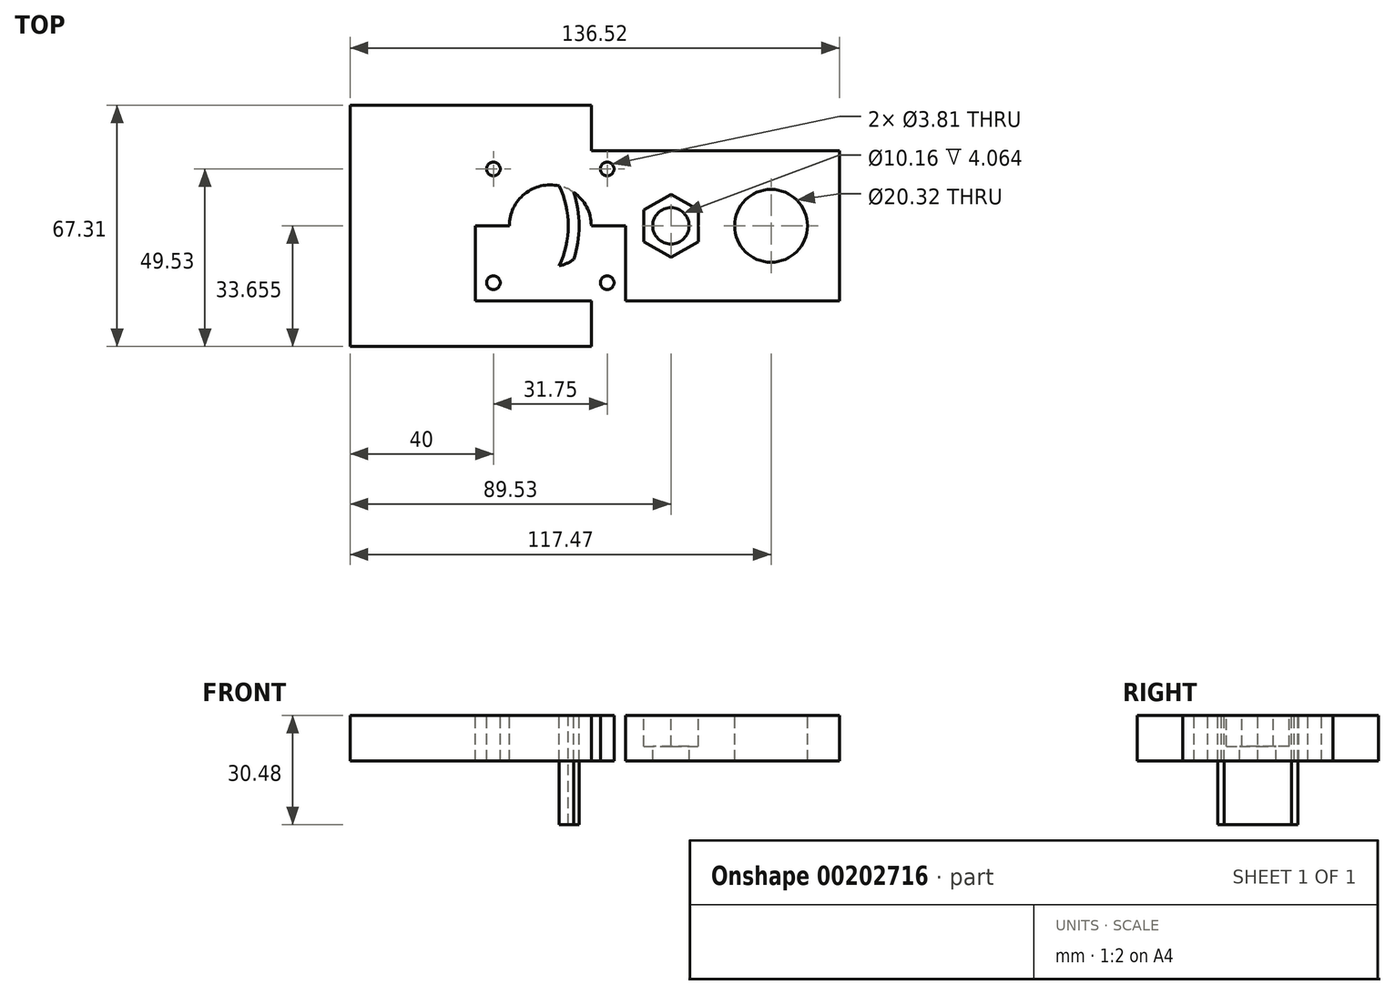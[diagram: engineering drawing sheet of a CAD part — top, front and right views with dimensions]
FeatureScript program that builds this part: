
annotation { "Feature Type Name" : "Feature", "Feature Type Description" : "" }
export const myFeature = defineFeature(function(context is Context, id is Id, definition is map)
    precondition{}
    {
        {
            var Q0;
            Q0=qCreatedBy(makeId("Top.planeOp"),FACE);
            var sketch = newSketch(context, id + "F0", { "sketchPlane" : qUnion([Q0])});
            skLineSegment(sketch, "E0.bottom", {"start": v(0, 0) * mm, "end": v(101.6, 0) * mm});
            skLineSegment(sketch, "E0.top", {"start": v(0, 41.91) * mm, "end": v(101.6, 41.91) * mm});
            skLineSegment(sketch, "E0.left", {"start": v(0, 0) * mm, "end": v(0, 41.91) * mm});
            skLineSegment(sketch, "E0.right", {"start": v(101.6, 0) * mm, "end": v(101.6, 41.91) * mm});
            skSolve(sketch);
        }
        {
            var Q0;
            Q0=makeQuery(id+"F0.imprint","IMPRINT",FACE,{"disambiguationData":[TD([[makeQuery(id+"F0.imprint","IMPRINT",EDGE,{"derivedFrom":sQuery(id+"F0.wireOp",EDGE,"E0.bottom")}),1.0]])]});
            extrude(context, id + "F1", {"entities" : qUnion([Q0]), "depth" : 12.7 * mm});
        }
        {
            var Q0;
            Q0=makeQuery(id+"F1.opExtrude","CAP_FACE",FACE,{"disambiguationData":[OSD([sQuery(id+"F0.wireOp",EDGE,"E0.bottom"),sQuery(id+"F0.wireOp",EDGE,"E0.top"),sQuery(id+"F0.wireOp",EDGE,"E0.left"),sQuery(id+"F0.wireOp",EDGE,"E0.right")])],"isStart":false});
            var sketch = newSketch(context, id + "F2", { "sketchPlane" : qUnion([Q0])});
            skLineSegment(sketch, "E1", {"start": v(0, 41.91) * mm, "end": v(5.08, 41.91) * mm});
            skLineSegment(sketch, "E2", {"start": v(5.08, 41.91) * mm, "end": v(5.08, 36.83) * mm});
            skLineSegment(sketch, "E3", {"start": v(0, 20.96) * mm, "end": v(101.6, 20.96) * mm});
            skLineSegment(sketch, "E4", {"start": v(0, 41.91) * mm, "end": v(41.91, 41.91) * mm});
            skLineSegment(sketch, "E5", {"start": v(41.91, 41.91) * mm, "end": v(41.91, 0) * mm});
            skLineSegment(sketch, "E6", {"start": v(41.91, 41.91) * mm, "end": v(36.83, 41.91) * mm});
            skLineSegment(sketch, "E7", {"start": v(36.83, 41.91) * mm, "end": v(36.83, 36.83) * mm});
            skLineSegment(sketch, "E8", {"start": v(41.91, 0) * mm, "end": v(41.91, 5.08) * mm});
            skCircle(sketch, "E9", {"center": v(36.83, 36.83) * mm, "radius": 1.9 * mm});
            skCircle(sketch, "E10", {"center": v(5.08, 36.83) * mm, "radius": 1.9 * mm});
            skCircle(sketch, "E11.MirrorC", {"center": v(36.83, 5.08) * mm, "radius": 1.9 * mm});
            skCircle(sketch, "E12.MirrorC", {"center": v(5.08, 5.08) * mm, "radius": 1.9 * mm});
            skSolve(sketch);
        }
        {
            var Q0;
            Q0=makeQuery(id+"F1.opExtrude","CAP_FACE",FACE,{"disambiguationData":[OSD([sQuery(id+"F0.wireOp",EDGE,"E0.bottom"),sQuery(id+"F0.wireOp",EDGE,"E0.top"),sQuery(id+"F0.wireOp",EDGE,"E0.left"),sQuery(id+"F0.wireOp",EDGE,"E0.right")])],"isStart":false});
            var sketch = newSketch(context, id + "F3", { "sketchPlane" : qUnion([Q0])});
            skLineSegment(sketch, "E13", {"start": v(0, 41.91) * mm, "end": v(41.91, 41.91) * mm});
            skLineSegment(sketch, "E14", {"start": v(41.91, 41.91) * mm, "end": v(41.91, 0) * mm});
            skLineSegment(sketch, "E15", {"start": v(41.91, 41.91) * mm, "end": v(54.61, 41.91) * mm});
            skLineSegment(sketch, "E16", {"start": v(54.61, 41.91) * mm, "end": v(54.61, 20.96) * mm});
            skCircle(sketch, "E17", {"center": v(54.61, 20.96) * mm, "radius": 5.08 * mm});
            skSolve(sketch);
        }
        {
            var Q0;
            Q0=makeQuery(id+"F3.imprint","IMPRINT",FACE,{"disambiguationData":[TD([[makeQuery(id+"F3.imprint","IMPRINT",EDGE,{"derivedFrom":sQuery(id+"F3.wireOp",EDGE,"E17")}),1.0]])]});
            extrude(context, id + "F4", {"entities" : qUnion([Q0]), "operationType" : NewBodyOperationType.REMOVE, "endBound" : BoundingType.THROUGH_ALL, "oppositeDirection" : true, "depth" : 25.4 * mm});
        }
        {
            var Q0;
            Q0=makeQuery(id+"F1.opExtrude","CAP_FACE",FACE,{"disambiguationData":[OSD([sQuery(id+"F0.wireOp",EDGE,"E0.bottom"),sQuery(id+"F0.wireOp",EDGE,"E0.top"),sQuery(id+"F0.wireOp",EDGE,"E0.left"),sQuery(id+"F0.wireOp",EDGE,"E0.right")])],"isStart":false});
            var sketch = newSketch(context, id + "F5", { "sketchPlane" : qUnion([Q0])});
            skLineSegment(sketch, "E18", {"start": v(54.61, 20.96) * mm, "end": v(62.23, 20.96) * mm});
            skCircle(sketch, "E19.cCircle", {"center": v(54.61, 20.96) * mm, "radius": 7.62 * mm, "construction": true});
            skLineSegment(sketch, "E19.0", {"start": v(62.23, 25.35) * mm, "end": v(62.23, 16.56) * mm});
            skLineSegment(sketch, "E19.1", {"start": v(62.23, 16.56) * mm, "end": v(54.61, 12.16) * mm});
            skLineSegment(sketch, "E19.2", {"start": v(54.61, 12.16) * mm, "end": v(46.99, 16.56) * mm});
            skLineSegment(sketch, "E19.3", {"start": v(47, 16.56) * mm, "end": v(47, 25.35) * mm});
            skLineSegment(sketch, "E19.4", {"start": v(47, 25.35) * mm, "end": v(54.6, 29.75) * mm});
            skLineSegment(sketch, "E19.5", {"start": v(54.6, 29.75) * mm, "end": v(62.23, 25.35) * mm});
            skPoint(sketch, "E19.0.midPoint", {"position": v(62.23, 20.96) * mm});
            skSolve(sketch);
        }
        {
            var Q0;
            {var subQ0=sQuery(id+"F5.wireOp",EDGE,"E19.1");Q0=makeQuery(id+"F5.imprint","IMPRINT",FACE,{"disambiguationData":[TD([[makeQuery(id+"F5.imprint","IMPRINT",EDGE,{"derivedFrom":subQ0}),-1.0]])]});}
            extrude(context, id + "F6", {"entities" : qUnion([Q0]), "operationType" : NewBodyOperationType.REMOVE, "oppositeDirection" : true, "depth" : 8.64 * mm});
        }
        {
            var Q0;
            Q0=makeQuery(id+"F1.opExtrude","CAP_FACE",FACE,{"disambiguationData":[OSD([sQuery(id+"F0.wireOp",EDGE,"E0.bottom"),sQuery(id+"F0.wireOp",EDGE,"E0.top"),sQuery(id+"F0.wireOp",EDGE,"E0.left"),sQuery(id+"F0.wireOp",EDGE,"E0.right")])],"isStart":false});
            var sketch = newSketch(context, id + "F7", { "sketchPlane" : qUnion([Q0])});
            skLineSegment(sketch, "E20", {"start": v(101.6, 20.96) * mm, "end": v(82.55, 20.96) * mm});
            skPoint(sketch, "E20.endSnap0", {"position": v(101.6, 20.96) * mm});
            skCircle(sketch, "E21", {"center": v(82.55, 20.96) * mm, "radius": 10.16 * mm});
            skSolve(sketch);
        }
        {
            var Q0;
            Q0=makeQuery(id+"F7.imprint","IMPRINT",FACE,{"disambiguationData":[TD([[makeQuery(id+"F7.imprint","IMPRINT",EDGE,{"derivedFrom":sQuery(id+"F7.wireOp",EDGE,"E21")}),1.0]])]});
            extrude(context, id + "F8", {"entities" : qUnion([Q0]), "operationType" : NewBodyOperationType.REMOVE, "endBound" : BoundingType.THROUGH_ALL, "oppositeDirection" : true, "depth" : 25.4 * mm});
        }
        {
            var Q0;
            Q0=makeQuery(id+"F1.opExtrude","CAP_FACE",FACE,{"disambiguationData":[OSD([sQuery(id+"F0.wireOp",EDGE,"E0.bottom"),sQuery(id+"F0.wireOp",EDGE,"E0.top"),sQuery(id+"F0.wireOp",EDGE,"E0.left"),sQuery(id+"F0.wireOp",EDGE,"E0.right")])],"isStart":false});
            var sketch = newSketch(context, id + "F9", { "sketchPlane" : qUnion([Q0])});
            skLineSegment(sketch, "E22", {"start": v(0, 41.91) * mm, "end": v(20.96, 41.91) * mm});
            skLineSegment(sketch, "E23", {"start": v(20.96, 41.91) * mm, "end": v(20.96, 20.96) * mm});
            skCircle(sketch, "E24", {"center": v(20.96, 20.96) * mm, "radius": 11.43 * mm});
            skSolve(sketch);
        }
        {
            var Q0;
            Q0 = qSketchRegion(id + "F9", true);
            extrude(context, id + "F10", {"entities" : qUnion([Q0]), "operationType" : NewBodyOperationType.REMOVE, "endBound" : BoundingType.THROUGH_ALL, "oppositeDirection" : true, "depth" : 25.4 * mm});
        }
        {
            var Q0;
            Q0=makeQuery(id+"F1.opExtrude","CAP_FACE",FACE,{"disambiguationData":[OSD([sQuery(id+"F0.wireOp",EDGE,"E0.bottom"),sQuery(id+"F0.wireOp",EDGE,"E0.top"),sQuery(id+"F0.wireOp",EDGE,"E0.left"),sQuery(id+"F0.wireOp",EDGE,"E0.right")])],"isStart":false});
            var sketch = newSketch(context, id + "F11", { "sketchPlane" : qUnion([Q0])});
            skLineSegment(sketch, "E25", {"start": v(32.39, 20.96) * mm, "end": v(32.39, -12.7) * mm});
            skLineSegment(sketch, "E26", {"start": v(32.39, 20.96) * mm, "end": v(32.39, 54.61) * mm});
            skLineSegment(sketch, "E27.bottom", {"start": v(32.38, -12.7) * mm, "end": v(-34.92, -12.7) * mm});
            skLineSegment(sketch, "E27.top", {"start": v(32.38, 54.61) * mm, "end": v(-34.93, 54.6) * mm});
            skLineSegment(sketch, "E27.left", {"start": v(32.39, -12.7) * mm, "end": v(32.39, 54.61) * mm});
            skLineSegment(sketch, "E27.right", {"start": v(-34.92, -12.7) * mm, "end": v(-34.93, 54.6) * mm});
            skSolve(sketch);
        }
        {
            var Q0;
            Q0=makeQuery(id+"F2.imprint","IMPRINT",FACE,{"disambiguationData":[TD([[makeQuery(id+"F2.imprint","IMPRINT",EDGE,{"derivedFrom":sQuery(id+"F2.wireOp",EDGE,"E9")}),1.0]])]});
            var Q1;
            Q1=makeQuery(id+"F2.imprint","IMPRINT",FACE,{"disambiguationData":[TD([[makeQuery(id+"F2.imprint","IMPRINT",EDGE,{"derivedFrom":sQuery(id+"F2.wireOp",EDGE,"E12.MirrorC")}),-1.0]])]});
            var Q2;
            Q2=makeQuery(id+"F2.imprint","IMPRINT",FACE,{"disambiguationData":[TD([[makeQuery(id+"F2.imprint","IMPRINT",EDGE,{"derivedFrom":sQuery(id+"F2.wireOp",EDGE,"E10")}),1.0]])]});
            var Q3;
            Q3=makeQuery(id+"F2.imprint","IMPRINT",FACE,{"disambiguationData":[TD([[makeQuery(id+"F2.imprint","IMPRINT",EDGE,{"derivedFrom":sQuery(id+"F2.wireOp",EDGE,"E11.MirrorC")}),-1.0]])]});
            extrude(context, id + "F12", {"entities" : qUnion([Q0, Q1, Q2, Q3]), "operationType" : NewBodyOperationType.REMOVE, "oppositeDirection" : true, "depth" : 25.4 * mm});
        }
        {
            var Q0;
            {var subQ7=sQuery(id+"F11.wireOp",EDGE,"E27.bottom");Q0=makeQuery(id+"F11.imprint","IMPRINT",FACE,{"disambiguationData":[TD([[makeQuery(id+"F11.imprint","IMPRINT",EDGE,{"derivedFrom":subQ7}),-1.0]])]});}
            extrude(context, id + "F13", {"entities" : qUnion([Q0]), "operationType" : NewBodyOperationType.ADD, "oppositeDirection" : true, "depth" : 12.7 * mm});
        }
        {
            var Q0;
            {var subQ0=sQuery(id+"F0.wireOp",EDGE,"E0.left");var subQ1=sQuery(id+"F0.wireOp",EDGE,"E0.top");var subQ2=sQuery(id+"F0.wireOp",EDGE,"E0.bottom");Q0=makeQuery(id+"F13.boolean.opBoolean","MERGE",FACE,{"derivedFrom":[makeQuery(id+"F1.opExtrude","CAP_FACE",FACE,{"disambiguationData":[OSD([subQ2,subQ1,subQ0,sQuery(id+"F0.wireOp",EDGE,"E0.right")])],"isStart":false}),makeQuery(id+"F13.opExtrude","CAP_FACE",FACE,{"disambiguationData":[OSD([subQ2,subQ1,subQ0,sQuery(id+"F11.wireOp",EDGE,"E27.bottom"),sQuery(id+"F11.wireOp",EDGE,"E27.top"),sQuery(id+"F11.wireOp",EDGE,"E27.left"),sQuery(id+"F11.wireOp",EDGE,"E27.right")])],"isStart":true})]});}
            var sketch = newSketch(context, id + "F14", { "sketchPlane" : qUnion([Q0])});
            skLineSegment(sketch, "E28", {"start": v(-34.93, 54.61) * mm, "end": v(0, 54.61) * mm});
            skCircle(sketch, "E29", {"center": v(0, 20.96) * mm, "radius": 29.03 * mm});
            skCircle(sketch, "E30", {"center": v(0, 20.96) * mm, "radius": 25.95 * mm});
            skCircle(sketch, "E31", {"center": v(20.96, 20.96) * mm, "radius": 11.43 * mm});
            skSolve(sketch);
        }
        {
            var Q0;
            {var subQ0=sQuery(id+"F14.wireOp",EDGE,"E31");var subQ1=sQuery(id+"F14.wireOp",EDGE,"E29");var subQ2=makeQuery(id+"F14.imprint","INTERSECT",VERTEX,{"disambiguationData":[OD(0.0)],"derivedFrom":[subQ1,subQ0]});Q0=makeQuery(id+"F14.imprint","IMPRINT",FACE,{"disambiguationData":[TD([[makeQuery(id+"F14.imprint","IMPRINT",EDGE,{"disambiguationData":[TD([[subQ2,-1.0]])],"derivedFrom":subQ1}),1.0]])]});}
            extrude(context, id + "F15", {"entities" : qUnion([Q0]), "operationType" : NewBodyOperationType.ADD, "oppositeDirection" : true, "depth" : 30.48 * mm});
        }
    });
